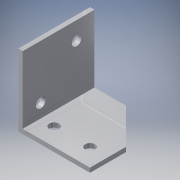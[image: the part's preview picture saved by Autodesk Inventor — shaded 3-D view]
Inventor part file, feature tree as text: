
AUTODESK INVENTOR PART (.ipt)
format: ipt  version: 2016 (Build 200138000, 138)  size: 124,928 bytes
history: native  units: in
note: dims shown in document units (in); Inventor stores cm internally (conversion verified against a paired STEP export)
features: extrude x3, sketch x3
ambient origin geometry x8: Origin, YZ Plane, XZ Plane, XY Plane, X Axis, Y Axis, Z Axis, Center Point
bodies: Solid1 (feature_tree)
feature tree (6):
  extrude  "Extrusion1"  Depth=0.125in
  sketch  "Sketch2"  dims[d2=1.875in d3=1.875in]
  extrude  "Extrusion3"  Depth=1.875in
  extrude  "Extrusion4"  Depth=0.125in
  sketch  "Sketch1"  dims[d0=2.0in d1=0.125in]
  sketch  "Sketch3"  dims[d4=2.0in d5=0.0in d6=0.875in d7=0.2656in d8=0.2656in d9=0.5in d10=0.5in d11=1.5in d12=1.5in d15=0.2656in d16=0.2656in d17=0.5in d18=0.5in d19=0.5in d20=0.5in d21=0.125in d22=0.0in d23=0.125in d24=0.0in]
